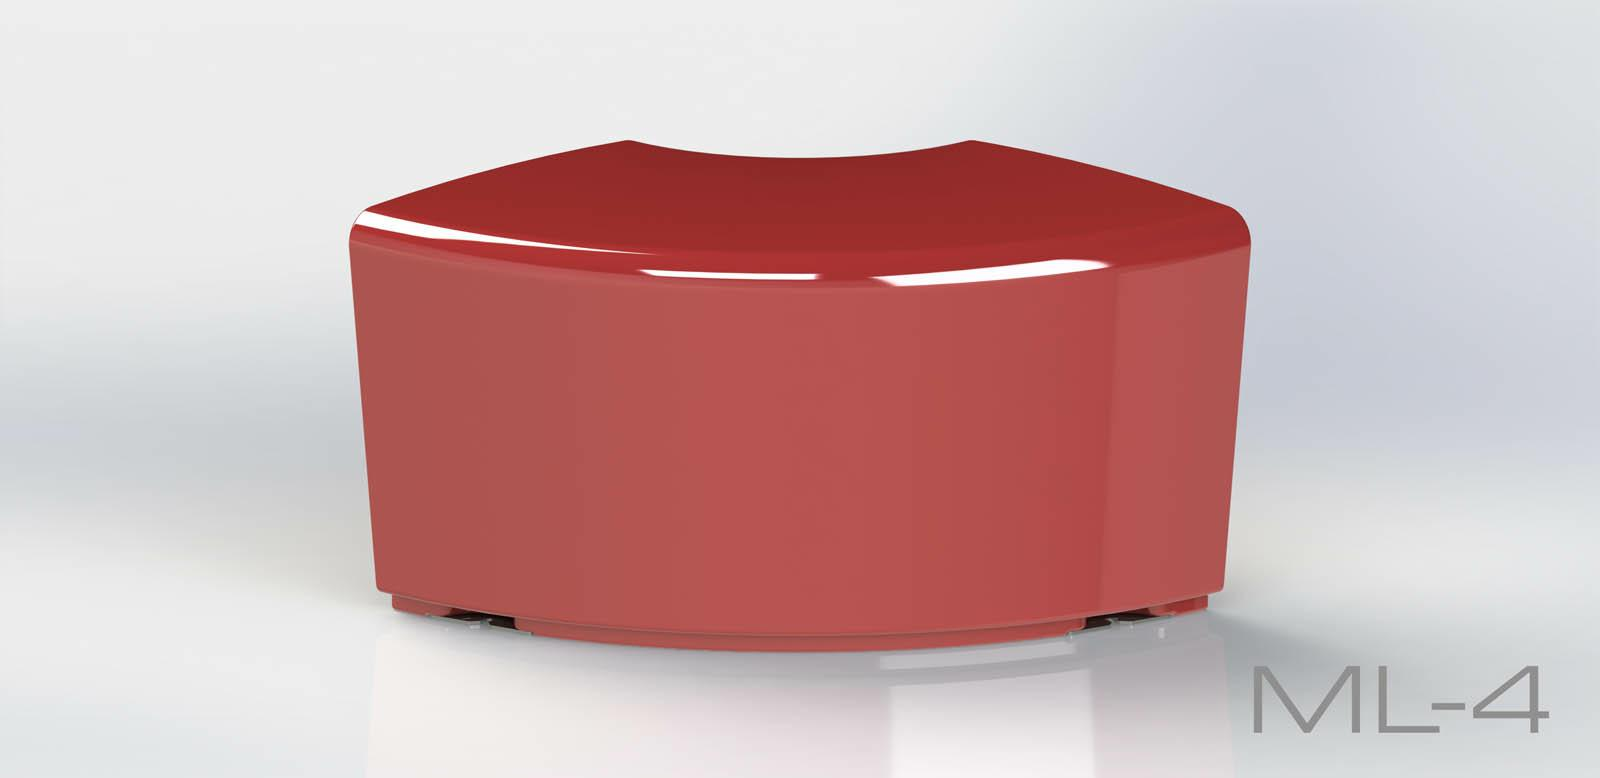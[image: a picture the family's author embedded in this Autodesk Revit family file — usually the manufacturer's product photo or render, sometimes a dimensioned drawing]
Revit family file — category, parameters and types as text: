
# Revit family: Modullaro ML 04
name_source: partatom
category: Furniture
revit_build: Autodesk Revit 2018 (Build: 20190510_1515(x64)
units: mm (PartAtom-declared; Revit-internal decimal feet)

## family parameters
Cut with Voids When Loaded = No
Host = Face
OmniClass Number = 23.40.10.11.14
OmniClass Title = Exterior Seating
Room Calculation Point = No
Shared = No

## types (1)
- Modullaro ML 04
    Default Elevation = 1219 mm
    Height = 500 mm  [stored 1.64042 ft]
    IfcExportAs = IfcFurnishingElement
    Length = 747 mm  [stored 2.45079 ft]
    Manufacturer = Astrini Design
    Material information = Colour choice from RAL colour standard. Customer may inquire about specific request regarding individual order.
    Model = Modullaro ML 04
    Operating temperature = -40°C to 80°C, ( -40°F to 176°F )
    Type Comments = Bench
    Type Image = ML-4.jpg
    URL = https://astrini-design.pl
    Weight (approximately) = 13.00 kg
    Width = 494 mm

note: [stored X ft] marks values corroborated as IEEE doubles in the binary element streams (Revit-internal decimal feet)
